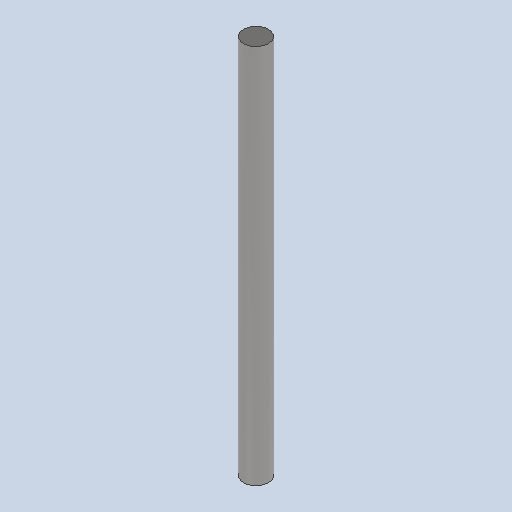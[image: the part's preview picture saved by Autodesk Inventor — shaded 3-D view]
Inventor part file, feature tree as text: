
AUTODESK INVENTOR PART (.ipt)
format: ipt  version: 2022 (Build 260153070, 153G)  size: 91,136 bytes
history: native  units: mm
features: extrude x1, sketch x1
ambient origin geometry x8: Origin, YZ Plane, XZ Plane, XY Plane, X Axis, Y Axis, Z Axis, Center Point
bodies: Solid1 (feature_tree)
feature tree (2):
  extrude  "Extrusion1"  Depth=152.4mm TaperAngle=0.0deg
  sketch  "Sketch1"  dims[d0=10.0mm d1=152.4mm d2=0.0mm]
